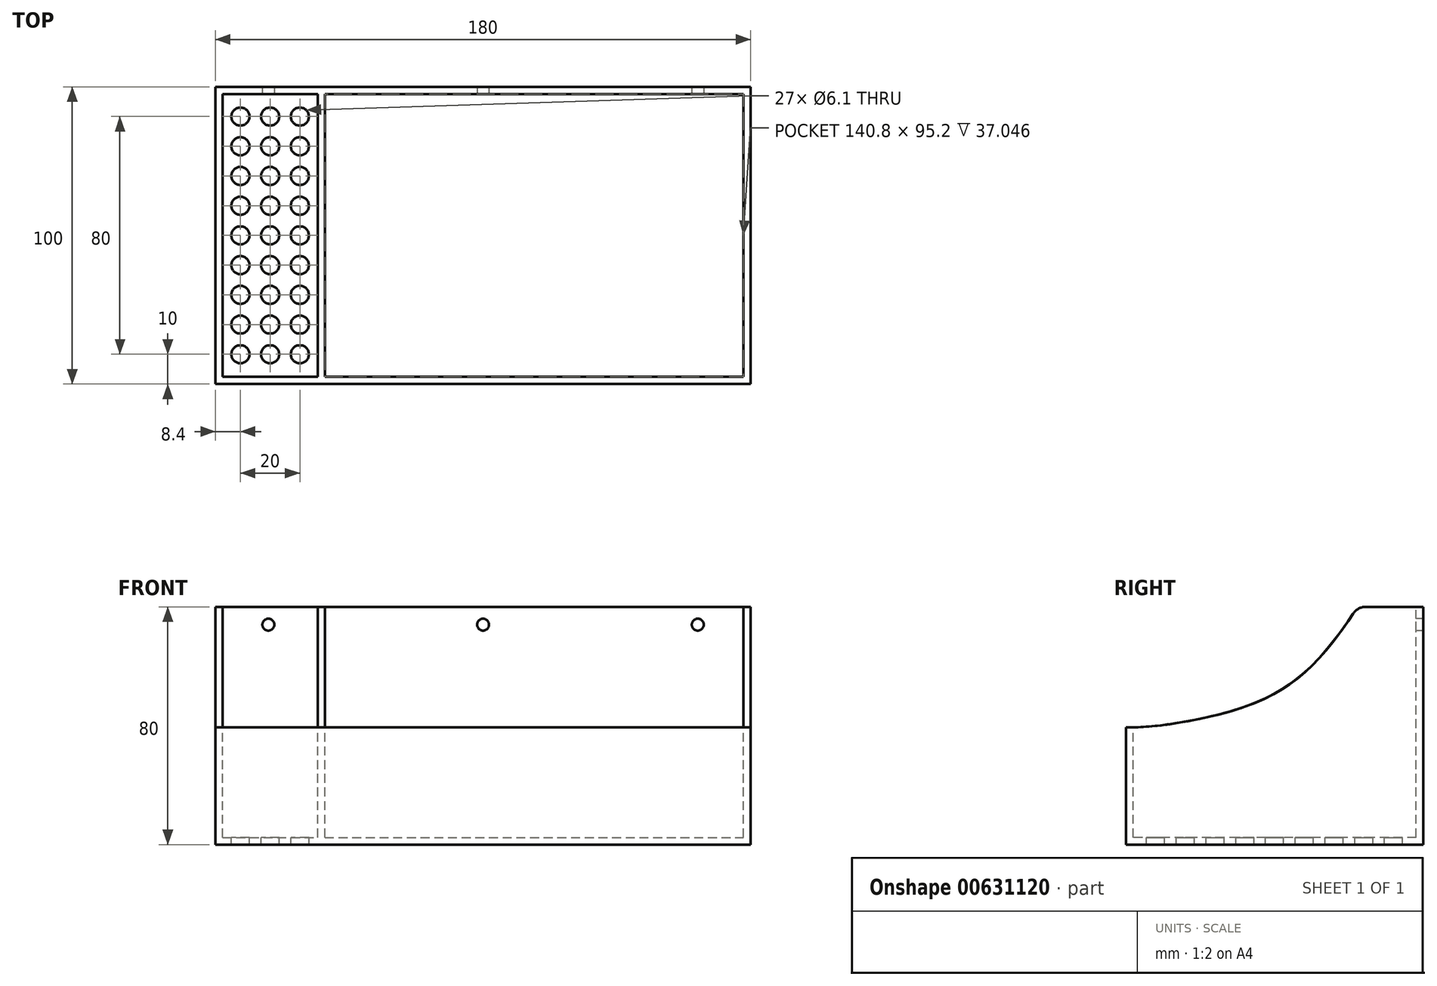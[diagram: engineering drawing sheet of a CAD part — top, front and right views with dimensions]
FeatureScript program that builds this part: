
annotation { "Feature Type Name" : "Feature", "Feature Type Description" : "" }
export const myFeature = defineFeature(function(context is Context, id is Id, definition is map)
    precondition{}
    {
        {
            assignVariable(context, id + "F0", {"variableType" : VariableType.LENGTH, "name" : "Wall", "lengthValue" : 2.4 * mm});
        }
        {
            var Q0;
            Q0=qCreatedBy(makeId("Top.planeOp"),FACE);
            var sketch = newSketch(context, id + "F1", { "sketchPlane" : qUnion([Q0])});
            skLineSegment(sketch, "E0.bottom", {"start": v(90, 50) * mm, "end": v(-90, 50) * mm});
            skLineSegment(sketch, "E0.top", {"start": v(90, -50) * mm, "end": v(-90, -50) * mm});
            skLineSegment(sketch, "E0.left", {"start": v(90, 50) * mm, "end": v(90, -50) * mm});
            skLineSegment(sketch, "E0.right", {"start": v(-90, 50) * mm, "end": v(-90, -50) * mm});
            skPoint(sketch, "E0.middle", {"position": v(0, 0) * mm});
            skSolve(sketch);
        }
        {
            var Q0;
            Q0 = qSketchRegion(id + "F1", true);
            extrude(context, id + "F2", {"entities" : qUnion([Q0]), "depth" : 80 * mm, "offsetDistance" : 25 * mm});
        }
        {
            var Q0;
            Q0=makeQuery(id+"F2.opExtrude","CAP_FACE",FACE,{"disambiguationData":[OSD([sQuery(id+"F1.wireOp",EDGE,"E0.bottom"),sQuery(id+"F1.wireOp",EDGE,"E0.top"),sQuery(id+"F1.wireOp",EDGE,"E0.left"),sQuery(id+"F1.wireOp",EDGE,"E0.right")])],"isStart":false});
            var sketch = newSketch(context, id + "F3", { "sketchPlane" : qUnion([Q0])});
            skLineSegment(sketch, "E1.bottom", {"start": v(-87.6, 47.6) * mm, "end": v(-55.6, 47.6) * mm});
            skLineSegment(sketch, "E1.top", {"start": v(-87.6, -47.6) * mm, "end": v(-55.6, -47.6) * mm});
            skLineSegment(sketch, "E1.left", {"start": v(-87.6, 47.6) * mm, "end": v(-87.6, -47.6) * mm});
            skLineSegment(sketch, "E1.right", {"start": v(-55.6, 47.6) * mm, "end": v(-55.6, -47.6) * mm});
            skLineSegment(sketch, "E2.bottom", {"start": v(-53.2, 47.6) * mm, "end": v(87.6, 47.6) * mm});
            skLineSegment(sketch, "E2.top", {"start": v(-53.2, -47.6) * mm, "end": v(87.6, -47.6) * mm});
            skLineSegment(sketch, "E2.left", {"start": v(-53.2, 47.6) * mm, "end": v(-53.2, -47.6) * mm});
            skLineSegment(sketch, "E2.right", {"start": v(87.6, 47.6) * mm, "end": v(87.6, -47.6) * mm});
            skSolve(sketch);
        }
        {
            var Q0;
            Q0 = qSketchRegion(id + "F3", true);
            extrude(context, id + "F4", {"entities" : qUnion([Q0]), "operationType" : NewBodyOperationType.REMOVE, "flatOperationType" : FlatOperationType.REMOVE, "oppositeDirection" : true, "depth" : 80 * mm - getVariable(context, 'Wall'), "offsetDistance" : 25 * mm, "domain" : OperationDomain.MODEL});
        }
        {
            var Q0;
            Q0=makeQuery(id+"F2.opExtrude","SWEPT_FACE",FACE,{"disambiguationData":[OSD([sQuery(id+"F1.wireOp",EDGE,"E0.left")])]});
            var sketch = newSketch(context, id + "F5", { "sketchPlane" : qUnion([Q0])});
            skPoint(sketch, "E3.1.internal.snap0", {"position": v(0, 0) * mm});
            skPoint(sketch, "E4.0.internal.snap0", {"position": v(-50, 40) * mm});
            skFitSpline(sketch, "E4", {"points": [v(-54.18, 40) * mm, v(-20.85, 43.26) * mm, v(11.9, 59.56) * mm, v(28.93, 81.78) * mm, v(28.78, 83.08) * mm, v(-48.7, 81.93) * mm, v(-56.34, 78.6) * mm, v(-58.22, 45.86) * mm, v(-54.18, 40) * mm]});
            skSolve(sketch);
        }
        {
            var Q0;
            Q0 = qSketchRegion(id + "F5", true);
            extrude(context, id + "F6", {"entities" : qUnion([Q0]), "operationType" : NewBodyOperationType.REMOVE, "endBound" : BoundingType.THROUGH_ALL, "oppositeDirection" : true, "depth" : 25 * mm, "offsetDistance" : 25 * mm});
        }
        {
            var Q0;
            Q0=makeQuery(id+"F4.boolean.opBoolean","COPY",FACE,{"derivedFrom":makeQuery(id+"F4.opExtrude","CAP_FACE",FACE,{"disambiguationData":[OSD([sQuery(id+"F3.wireOp",EDGE,"E1.bottom"),sQuery(id+"F3.wireOp",EDGE,"E1.top"),sQuery(id+"F3.wireOp",EDGE,"E1.left"),sQuery(id+"F3.wireOp",EDGE,"E1.right")])],"isStart":false})});
            var sketch = newSketch(context, id + "F7", { "sketchPlane" : qUnion([Q0])});
            skCircle(sketch, "E5", {"center": v(-81.6, 40) * mm, "radius": 3.05 * mm});
            skCircle(sketch, "E6.0.1.0", {"center": v(-81.6, 30) * mm, "radius": 3.05 * mm});
            skCircle(sketch, "E6.0.2.0", {"center": v(-81.6, 20) * mm, "radius": 3.05 * mm});
            skCircle(sketch, "E6.0.3.0", {"center": v(-81.6, 10) * mm, "radius": 3.05 * mm});
            skCircle(sketch, "E6.0.4.0", {"center": v(-81.6, 0) * mm, "radius": 3.05 * mm});
            skCircle(sketch, "E6.0.5.0", {"center": v(-81.6, -10) * mm, "radius": 3.05 * mm});
            skCircle(sketch, "E6.0.6.0", {"center": v(-81.6, -20) * mm, "radius": 3.05 * mm});
            skCircle(sketch, "E6.0.7.0", {"center": v(-81.6, -30) * mm, "radius": 3.05 * mm});
            skCircle(sketch, "E6.0.8.0", {"center": v(-81.6, -40) * mm, "radius": 3.05 * mm});
            skCircle(sketch, "E6.1.0.0", {"center": v(-71.6, 40) * mm, "radius": 3.05 * mm});
            skCircle(sketch, "E6.1.1.0", {"center": v(-71.6, 30) * mm, "radius": 3.05 * mm});
            skCircle(sketch, "E6.1.2.0", {"center": v(-71.6, 20) * mm, "radius": 3.05 * mm});
            skCircle(sketch, "E6.1.3.0", {"center": v(-71.6, 10) * mm, "radius": 3.05 * mm});
            skCircle(sketch, "E6.1.4.0", {"center": v(-71.6, 0) * mm, "radius": 3.05 * mm});
            skCircle(sketch, "E6.1.5.0", {"center": v(-71.6, -10) * mm, "radius": 3.05 * mm});
            skCircle(sketch, "E6.1.6.0", {"center": v(-71.6, -20) * mm, "radius": 3.05 * mm});
            skCircle(sketch, "E6.1.7.0", {"center": v(-71.6, -30) * mm, "radius": 3.05 * mm});
            skCircle(sketch, "E6.1.8.0", {"center": v(-71.6, -40) * mm, "radius": 3.05 * mm});
            skCircle(sketch, "E6.2.0.0", {"center": v(-61.6, 40) * mm, "radius": 3.05 * mm});
            skCircle(sketch, "E6.2.1.0", {"center": v(-61.6, 30) * mm, "radius": 3.05 * mm});
            skCircle(sketch, "E6.2.2.0", {"center": v(-61.6, 20) * mm, "radius": 3.05 * mm});
            skCircle(sketch, "E6.2.3.0", {"center": v(-61.6, 10) * mm, "radius": 3.05 * mm});
            skCircle(sketch, "E6.2.4.0", {"center": v(-61.6, 0) * mm, "radius": 3.05 * mm});
            skCircle(sketch, "E6.2.5.0", {"center": v(-61.6, -10) * mm, "radius": 3.05 * mm});
            skCircle(sketch, "E6.2.6.0", {"center": v(-61.6, -20) * mm, "radius": 3.05 * mm});
            skCircle(sketch, "E6.2.7.0", {"center": v(-61.6, -30) * mm, "radius": 3.05 * mm});
            skCircle(sketch, "E6.2.8.0", {"center": v(-61.6, -40) * mm, "radius": 3.05 * mm});
            skLineSegment(sketch, "E6.direction1", {"start": v(-81.6, 40) * mm, "end": v(-71.6, 40) * mm, "construction": true});
            skLineSegment(sketch, "E6.direction2", {"start": v(-81.6, 40) * mm, "end": v(-81.6, 30) * mm, "construction": true});
            skLineSegment(sketch, "E7", {"start": v(-55.6, 47.6) * mm, "end": v(-87.6, -47.6) * mm, "construction": true});
            skLineSegment(sketch, "E8", {"start": v(-55.6, -47.6) * mm, "end": v(-87.6, 47.6) * mm, "construction": true});
            skLineSegment(sketch, "E9", {"start": v(-71.6, 0) * mm, "end": v(-71.6, -4.64) * mm, "construction": true});
            skSolve(sketch);
        }
        {
            var Q0;
            Q0 = qSketchRegion(id + "F7", true);
            extrude(context, id + "F8", {"entities" : qUnion([Q0]), "operationType" : NewBodyOperationType.REMOVE, "endBound" : BoundingType.THROUGH_ALL, "oppositeDirection" : true, "depth" : 25 * mm, "offsetDistance" : 25 * mm});
        }
        {
            var Q0;
            Q0=makeQuery(id+"F4.boolean.opBoolean","COPY",FACE,{"derivedFrom":makeQuery(id+"F4.opExtrude","SWEPT_FACE",FACE,{"disambiguationData":[OSD([sQuery(id+"F3.wireOp",EDGE,"E1.bottom")])]})});
            var sketch = newSketch(context, id + "F9", { "sketchPlane" : qUnion([Q0])});
            skCircle(sketch, "E10", {"center": v(-72.2, 74) * mm, "radius": 2 * mm});
            skCircle(sketch, "E11.MirrorC", {"center": v(72.2, 74) * mm, "radius": 2 * mm});
            skLineSegment(sketch, "E12", {"start": v(-71.6, 80) * mm, "end": v(-71.6, 80.62) * mm, "construction": true});
            skPoint(sketch, "E12.endSnap0", {"position": v(-71.6, 80) * mm});
            skCircle(sketch, "E13", {"center": v(0, 74) * mm, "radius": 2 * mm});
            skSolve(sketch);
        }
        {
            var Q0;
            Q0 = qSketchRegion(id + "F9", true);
            extrude(context, id + "F10", {"entities" : qUnion([Q0]), "operationType" : NewBodyOperationType.REMOVE, "endBound" : BoundingType.THROUGH_ALL, "oppositeDirection" : true, "depth" : 25 * mm, "offsetDistance" : 25 * mm});
        }
        {
            var Q0;
            Q0=makeQuery(id+"F6.boolean.opBoolean","INTERSECT",EDGE,{"disambiguationData":[OD(1.0)],"derivedFrom":[makeQuery(id+"F2.opExtrude","CAP_FACE",FACE,{"disambiguationData":[OSD([sQuery(id+"F1.wireOp",EDGE,"E0.bottom"),sQuery(id+"F1.wireOp",EDGE,"E0.top"),sQuery(id+"F1.wireOp",EDGE,"E0.left"),sQuery(id+"F1.wireOp",EDGE,"E0.right")])],"isStart":false}),makeQuery(id+"F6.opExtrude","SWEPT_FACE",FACE,{"disambiguationData":[OSD([sQuery(id+"F5.wireOp",EDGE,"E4")])]})]});
            var Q1;
            Q1=makeQuery(id+"F6.boolean.opBoolean","INTERSECT",EDGE,{"disambiguationData":[OD(2.0)],"derivedFrom":[makeQuery(id+"F2.opExtrude","CAP_FACE",FACE,{"disambiguationData":[OSD([sQuery(id+"F1.wireOp",EDGE,"E0.bottom"),sQuery(id+"F1.wireOp",EDGE,"E0.top"),sQuery(id+"F1.wireOp",EDGE,"E0.left"),sQuery(id+"F1.wireOp",EDGE,"E0.right")])],"isStart":false}),makeQuery(id+"F6.opExtrude","SWEPT_FACE",FACE,{"disambiguationData":[OSD([sQuery(id+"F5.wireOp",EDGE,"E4")])]})]});
            var Q2;
            Q2=makeQuery(id+"F6.boolean.opBoolean","INTERSECT",EDGE,{"disambiguationData":[OD(0.0)],"derivedFrom":[makeQuery(id+"F2.opExtrude","CAP_FACE",FACE,{"disambiguationData":[OSD([sQuery(id+"F1.wireOp",EDGE,"E0.bottom"),sQuery(id+"F1.wireOp",EDGE,"E0.top"),sQuery(id+"F1.wireOp",EDGE,"E0.left"),sQuery(id+"F1.wireOp",EDGE,"E0.right")])],"isStart":false}),makeQuery(id+"F6.opExtrude","SWEPT_FACE",FACE,{"disambiguationData":[OSD([sQuery(id+"F5.wireOp",EDGE,"E4")])]})]});
            fillet(context, id + "F11", {"entities" : qUnion([Q0, Q1, Q2]), "radius" : 5 * mm, "tangentPropagation" : true, "allowEdgeOverflow" : false});
        }
    });
